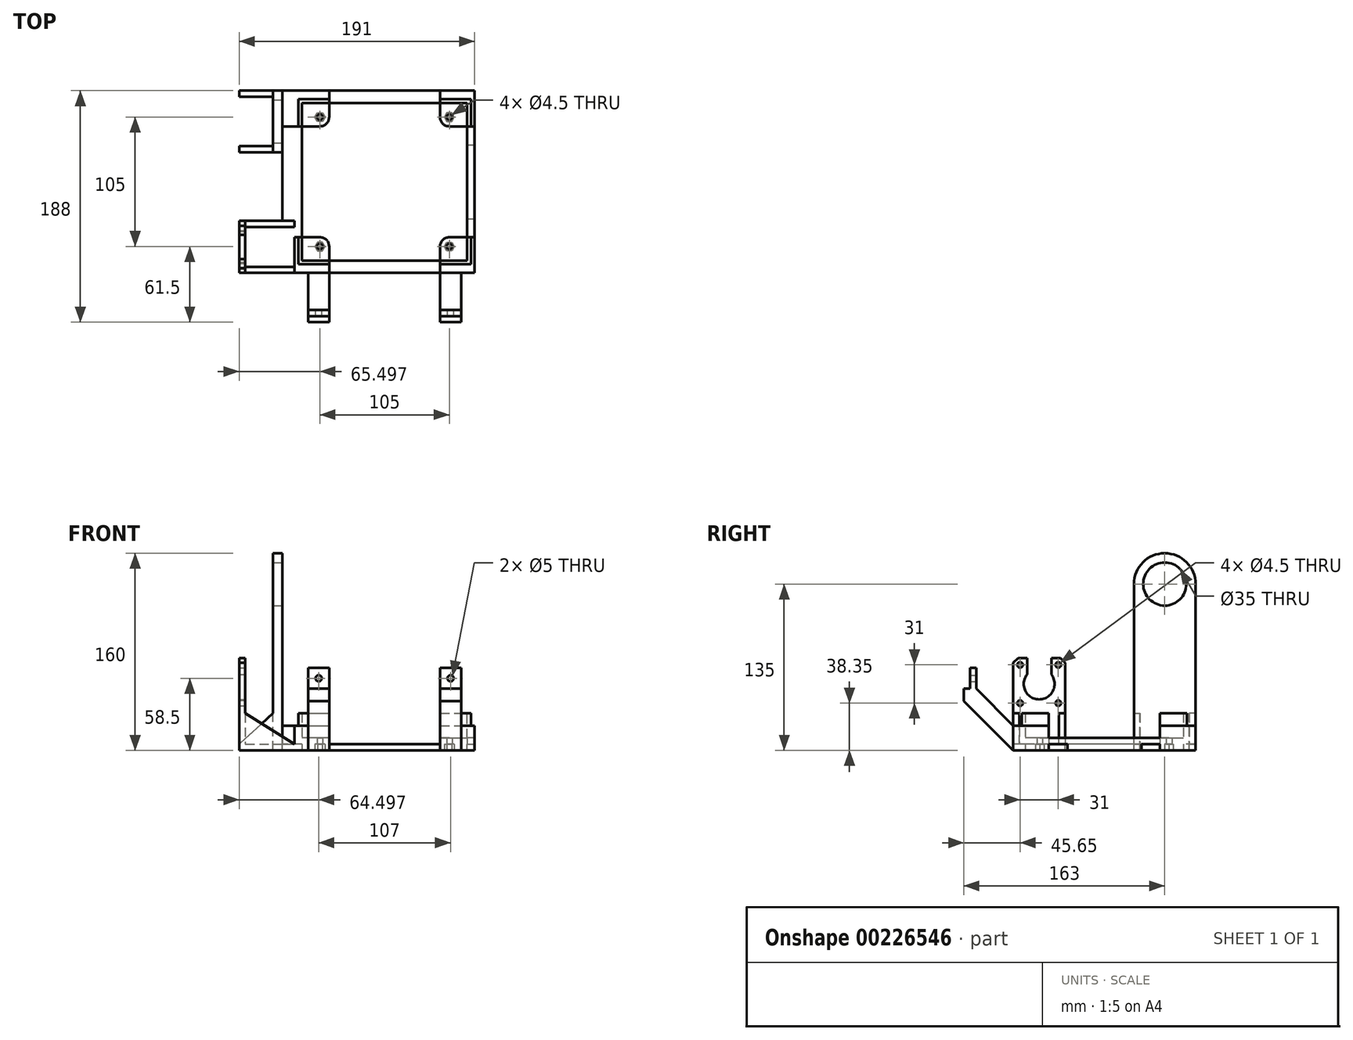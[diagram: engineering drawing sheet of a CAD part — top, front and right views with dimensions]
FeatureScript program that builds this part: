
annotation { "Feature Type Name" : "Feature", "Feature Type Description" : "" }
export const myFeature = defineFeature(function(context is Context, id is Id, definition is map)
    precondition{}
    {
        {
            var Q0;
            Q0=qCreatedBy(makeId("Top.planeOp"),FACE);
            var sketch = newSketch(context, id + "F0", { "sketchPlane" : qUnion([Q0])});
            skLineSegment(sketch, "E0.bottom", {"start": v(3.28, 0) * mm, "end": v(149.28, 0) * mm});
            skLineSegment(sketch, "E0.top", {"start": v(3.28, 148) * mm, "end": v(149.28, 148) * mm});
            skLineSegment(sketch, "E0.left", {"start": v(3.28, 0) * mm, "end": v(3.28, 148) * mm});
            skLineSegment(sketch, "E0.right", {"start": v(149.28, 0) * mm, "end": v(149.28, 148) * mm});
            skLineSegment(sketch, "E1.bottom", {"start": v(9.28, 10) * mm, "end": v(143.28, 10) * mm});
            skLineSegment(sketch, "E1.top", {"start": v(9.28, 138) * mm, "end": v(143.28, 138) * mm});
            skLineSegment(sketch, "E1.left", {"start": v(9.28, 10) * mm, "end": v(9.28, 138) * mm});
            skLineSegment(sketch, "E1.right", {"start": v(143.28, 10) * mm, "end": v(143.28, 138) * mm});
            skSolve(sketch);
        }
        {
            var Q0;
            Q0 = qSketchRegion(id + "F0", true);
            extrude(context, id + "F1", {"entities" : qUnion([Q0]), "depth" : 20 * mm});
        }
        {
            var Q0;
            Q0=makeQuery(id+"F1.opExtrude","CAP_FACE",FACE,{"disambiguationData":[OSD([sQuery(id+"F0.wireOp",EDGE,"E0.bottom"),sQuery(id+"F0.wireOp",EDGE,"E0.top"),sQuery(id+"F0.wireOp",EDGE,"E0.left"),sQuery(id+"F0.wireOp",EDGE,"E0.right"),sQuery(id+"F0.wireOp",EDGE,"E1.bottom"),sQuery(id+"F0.wireOp",EDGE,"E1.top"),sQuery(id+"F0.wireOp",EDGE,"E1.left"),sQuery(id+"F0.wireOp",EDGE,"E1.right")])],"isStart":false});
            var sketch = newSketch(context, id + "F2", { "sketchPlane" : qUnion([Q0])});
            skLineSegment(sketch, "E2.0", {"start": v(6.28, 141) * mm, "end": v(146.28, 141) * mm});
            skLineSegment(sketch, "E2.1", {"start": v(6.28, 7) * mm, "end": v(6.28, 141) * mm});
            skLineSegment(sketch, "E2.2", {"start": v(6.28, 7) * mm, "end": v(146.28, 7) * mm});
            skLineSegment(sketch, "E2.3", {"start": v(146.28, 7) * mm, "end": v(146.28, 141) * mm});
            skLineSegment(sketch, "E3.0", {"start": v(9.28, 10) * mm, "end": v(9.28, 138) * mm});
            skLineSegment(sketch, "E4.0", {"start": v(9.28, 138) * mm, "end": v(143.28, 138) * mm});
            skLineSegment(sketch, "E5.0", {"start": v(143.28, 10) * mm, "end": v(143.28, 138) * mm});
            skLineSegment(sketch, "E6.0", {"start": v(9.28, 10) * mm, "end": v(143.28, 10) * mm});
            skSolve(sketch);
        }
        {
            var Q0;
            Q0 = qSketchRegion(id + "F2", true);
            extrude(context, id + "F3", {"entities" : qUnion([Q0]), "operationType" : NewBodyOperationType.ADD, "depth" : 10 * mm});
        }
        {
            var Q0;
            Q0=qCreatedBy(makeId("Right.planeOp"),FACE);
            var sketch = newSketch(context, id + "F4", { "sketchPlane" : qUnion([Q0])});
            skLineSegment(sketch, "E7.0", {"start": v(7, 30) * mm, "end": v(141, 30) * mm, "construction": true});
            skPoint(sketch, "E8.0", {"position": v(141, 25) * mm});
            skLineSegment(sketch, "E9.0", {"start": v(141, 30) * mm, "end": v(141, 20) * mm, "construction": true});
            skLineSegment(sketch, "E10.0", {"start": v(0, 20) * mm, "end": v(148, 20) * mm, "construction": true});
            skLineSegment(sketch, "E11.0", {"start": v(148, 20) * mm, "end": v(148, 0) * mm, "construction": true});
            skLineSegment(sketch, "E12.0", {"start": v(0, 0) * mm, "end": v(148, 0) * mm, "construction": true});
            skLineSegment(sketch, "E13.0", {"start": v(0, 20) * mm, "end": v(0, 0) * mm, "construction": true});
            skLineSegment(sketch, "E14.0", {"start": v(7, 30) * mm, "end": v(7, 20) * mm, "construction": true});
            skLineSegment(sketch, "E15", {"start": v(119, 30) * mm, "end": v(119, 5) * mm});
            skLineSegment(sketch, "E16", {"start": v(119, 5) * mm, "end": v(29, 5) * mm});
            skLineSegment(sketch, "E17", {"start": v(29, 5) * mm, "end": v(29, 30) * mm});
            skLineSegment(sketch, "E18", {"start": v(29, 30) * mm, "end": v(119, 30) * mm});
            skSolve(sketch);
        }
        {
            var Q0;
            Q0 = qSketchRegion(id + "F4", true);
            extrude(context, id + "F5", {"entities" : qUnion([Q0]), "operationType" : NewBodyOperationType.REMOVE, "endBound" : BoundingType.THROUGH_ALL, "depth" : 25 * mm});
        }
        {
            var Q0;
            Q0=qCreatedBy(makeId("Front.planeOp"),FACE);
            var sketch = newSketch(context, id + "F6", { "sketchPlane" : qUnion([Q0])});
            skLineSegment(sketch, "E19.0", {"start": v(6.28, 30) * mm, "end": v(6.28, 20) * mm, "construction": true});
            skLineSegment(sketch, "E20.0", {"start": v(6.28, 30) * mm, "end": v(146.28, 30) * mm, "construction": true});
            skLineSegment(sketch, "E21.0", {"start": v(3.28, 20) * mm, "end": v(3.28, 0) * mm, "construction": true});
            skLineSegment(sketch, "E22.0", {"start": v(3.28, 20) * mm, "end": v(149.28, 20) * mm, "construction": true});
            skLineSegment(sketch, "E23.0", {"start": v(146.28, 30) * mm, "end": v(146.28, 20) * mm, "construction": true});
            skLineSegment(sketch, "E24.0", {"start": v(149.28, 20) * mm, "end": v(149.28, 0) * mm, "construction": true});
            skLineSegment(sketch, "E25", {"start": v(31.28, 30) * mm, "end": v(121.28, 30) * mm});
            skLineSegment(sketch, "E26", {"start": v(31.28, 5) * mm, "end": v(31.28, 30) * mm});
            skLineSegment(sketch, "E27", {"start": v(31.28, 5) * mm, "end": v(121.28, 5) * mm});
            skLineSegment(sketch, "E28", {"start": v(121.28, 5) * mm, "end": v(121.28, 30) * mm});
            skSolve(sketch);
        }
        {
            var Q0;
            Q0 = qSketchRegion(id + "F6", true);
            extrude(context, id + "F7", {"entities" : qUnion([Q0]), "operationType" : NewBodyOperationType.REMOVE, "endBound" : BoundingType.THROUGH_ALL, "oppositeDirection" : true, "depth" : 25 * mm});
        }
        {
            var Q0;
            Q0=makeQuery(id+"F1.opExtrude","SWEPT_FACE",FACE,{"disambiguationData":[OSD([sQuery(id+"F0.wireOp",EDGE,"E0.bottom")])]});
            var sketch = newSketch(context, id + "F8", { "sketchPlane" : qUnion([Q0])});
            skPoint(sketch, "E29.firstSnap0", {"position": v(31.28, 12.5) * mm});
            skLineSegment(sketch, "E29.bottom", {"start": v(31.28, 0) * mm, "end": v(14.28, 0) * mm});
            skLineSegment(sketch, "E29.top", {"start": v(31.28, 67) * mm, "end": v(14.28, 67) * mm});
            skLineSegment(sketch, "E29.left", {"start": v(31.28, 0) * mm, "end": v(31.28, 67) * mm});
            skLineSegment(sketch, "E29.right", {"start": v(14.28, 0) * mm, "end": v(14.28, 67) * mm});
            skLineSegment(sketch, "E30.bottom", {"start": v(121.28, 0) * mm, "end": v(138.28, 0) * mm});
            skLineSegment(sketch, "E30.top", {"start": v(121.28, 67) * mm, "end": v(138.28, 67) * mm});
            skLineSegment(sketch, "E30.left", {"start": v(121.28, 0) * mm, "end": v(121.28, 67) * mm});
            skLineSegment(sketch, "E30.right", {"start": v(138.28, 0) * mm, "end": v(138.28, 67) * mm});
            skLineSegment(sketch, "E31.0", {"start": v(6.28, 30) * mm, "end": v(31.28, 30) * mm, "construction": true});
            skCircle(sketch, "E32", {"center": v(22.78, 58.5) * mm, "radius": 2.5 * mm});
            skCircle(sketch, "E33", {"center": v(129.78, 58.5) * mm, "radius": 2.5 * mm});
            skSolve(sketch);
        }
        {
            var Q0;
            Q0 = qSketchRegion(id + "F8", true);
            extrude(context, id + "F9", {"entities" : qUnion([Q0]), "operationType" : NewBodyOperationType.ADD, "depth" : 40 * mm});
        }
        {
            var Q0;
            Q0=makeQuery(id+"F9.opExtrude","SWEPT_FACE",FACE,{"disambiguationData":[OSD([sQuery(id+"F8.wireOp",EDGE,"E29.right")])]});
            var sketch = newSketch(context, id + "F10", { "sketchPlane" : qUnion([Q0])});
            skLineSegment(sketch, "E34", {"start": v(0, 20) * mm, "end": v(30, 50) * mm});
            skLineSegment(sketch, "E35", {"start": v(30, 50) * mm, "end": v(30, 67) * mm});
            skLineSegment(sketch, "E36", {"start": v(30, 67) * mm, "end": v(0, 67) * mm});
            skLineSegment(sketch, "E37", {"start": v(0, 67) * mm, "end": v(0, 20) * mm});
            skLineSegment(sketch, "E38.bottom", {"start": v(40, 67) * mm, "end": v(35, 67) * mm});
            skLineSegment(sketch, "E38.top", {"start": v(40, 50) * mm, "end": v(35, 50) * mm});
            skLineSegment(sketch, "E38.left", {"start": v(40, 67) * mm, "end": v(40, 50) * mm});
            skLineSegment(sketch, "E38.right", {"start": v(35, 67) * mm, "end": v(35, 50) * mm});
            skLineSegment(sketch, "E39", {"start": v(0, 0) * mm, "end": v(40, 40) * mm});
            skLineSegment(sketch, "E40", {"start": v(40, 40) * mm, "end": v(40, 0) * mm});
            skLineSegment(sketch, "E41", {"start": v(40, 0) * mm, "end": v(0, 0) * mm});
            skSolve(sketch);
        }
        {
            var Q0;
            Q0 = qSketchRegion(id + "F10", true);
            extrude(context, id + "F11", {"entities" : qUnion([Q0]), "operationType" : NewBodyOperationType.REMOVE, "endBound" : BoundingType.THROUGH_ALL, "oppositeDirection" : true, "depth" : 25 * mm});
        }
        {
            var Q0;
            Q0=makeQuery(id+"F1.opExtrude","SWEPT_FACE",FACE,{"disambiguationData":[OSD([sQuery(id+"F0.wireOp",EDGE,"E0.left")])]});
            var sketch = newSketch(context, id + "F12", { "sketchPlane" : qUnion([Q0])});
            skLineSegment(sketch, "E42.bottom", {"start": v(0, 0) * mm, "end": v(-148, 0) * mm});
            skLineSegment(sketch, "E42.top", {"start": v(0, 5) * mm, "end": v(-148, 5) * mm});
            skLineSegment(sketch, "E42.left", {"start": v(0, 0) * mm, "end": v(0, 5) * mm});
            skLineSegment(sketch, "E42.right", {"start": v(-148, 0) * mm, "end": v(-148, 5) * mm});
            skSolve(sketch);
        }
        {
            var Q0;
            Q0 = qSketchRegion(id + "F12", true);
            extrude(context, id + "F13", {"entities" : qUnion([Q0]), "operationType" : NewBodyOperationType.ADD, "depth" : 10 * mm});
        }
        {
            var Q0;
            Q0=makeQuery(id+"F13.opExtrude","CAP_FACE",FACE,{"disambiguationData":[OSD([sQuery(id+"F12.wireOp",EDGE,"E42.bottom"),sQuery(id+"F12.wireOp",EDGE,"E42.top"),sQuery(id+"F12.wireOp",EDGE,"E42.left"),sQuery(id+"F12.wireOp",EDGE,"E42.right")])],"isStart":false});
            var sketch = newSketch(context, id + "F14", { "sketchPlane" : qUnion([Q0])});
            skLineSegment(sketch, "E43.bottom", {"start": v(-148, 0) * mm, "end": v(-98, 0) * mm});
            skLineSegment(sketch, "E43.left", {"start": v(-148, 0) * mm, "end": v(-148, 135) * mm});
            skLineSegment(sketch, "E43.right", {"start": v(-98, 0) * mm, "end": v(-98, 135) * mm});
            skArc(sketch, "E44", {"start": v(-98, 135) * mm, "mid": v(-123, 160) * mm, "end": v(-148, 135) * mm});
            skCircle(sketch, "E45", {"center": v(-123, 135) * mm, "radius": 17.5 * mm});
            skSolve(sketch);
        }
        {
            var Q0;
            Q0 = qSketchRegion(id + "F14", true);
            extrude(context, id + "F15", {"entities" : qUnion([Q0]), "operationType" : NewBodyOperationType.ADD, "depth" : 7.5 * mm});
        }
        {
            var Q0;
            Q0=makeQuery(id+"F13.boolean.opBoolean","MERGE",FACE,{"derivedFrom":[makeQuery(id+"F5.boolean.opBoolean","COPY",FACE,{"disambiguationData":[TD([makeQuery(id+"F1.opExtrude","SWEPT_FACE",FACE,{"disambiguationData":[OSD([sQuery(id+"F0.wireOp",EDGE,"E0.left")])]})])],"derivedFrom":makeQuery(id+"F5.opExtrude","SWEPT_FACE",FACE,{"disambiguationData":[OSD([sQuery(id+"F4.wireOp",EDGE,"E16")])]})}),makeQuery(id+"F13.opExtrude","SWEPT_FACE",FACE,{"disambiguationData":[OSD([sQuery(id+"F12.wireOp",EDGE,"E42.top")])]})]});
            var sketch = newSketch(context, id + "F16", { "sketchPlane" : qUnion([Q0])});
            skLineSegment(sketch, "E46.bottom", {"start": v(3.28, 148) * mm, "end": v(-6.72, 148) * mm});
            skLineSegment(sketch, "E46.top", {"start": v(3.28, 119) * mm, "end": v(-6.72, 119) * mm});
            skLineSegment(sketch, "E46.left", {"start": v(3.28, 148) * mm, "end": v(3.28, 119) * mm});
            skLineSegment(sketch, "E46.right", {"start": v(-6.72, 148) * mm, "end": v(-6.72, 119) * mm});
            skSolve(sketch);
        }
        {
            var Q0;
            Q0 = qSketchRegion(id + "F16", true);
            var Q1;
            {var subQ4=sQuery(id+"F0.wireOp",EDGE,"E0.left");var subQ5=makeQuery(id+"F1.opExtrude","SWEPT_FACE",FACE,{"disambiguationData":[OSD([subQ4])]});var subQ6=sQuery(id+"F0.wireOp",EDGE,"E0.top");var subQ7=makeQuery(id+"F1.opExtrude","SWEPT_FACE",FACE,{"disambiguationData":[OSD([subQ6])]});var subQ10=sQuery(id+"F0.wireOp",EDGE,"E1.left");var subQ11=sQuery(id+"F0.wireOp",EDGE,"E0.right");var subQ12=makeQuery(id+"F1.opExtrude","CAP_FACE",FACE,{"disambiguationData":[OSD([sQuery(id+"F0.wireOp",EDGE,"E0.bottom"),subQ6,subQ4,subQ11,sQuery(id+"F0.wireOp",EDGE,"E1.bottom"),sQuery(id+"F0.wireOp",EDGE,"E1.top"),subQ10,sQuery(id+"F0.wireOp",EDGE,"E1.right")])],"isStart":false});Q1=makeQuery(id+"F7.boolean.opBoolean","SPLIT",FACE,{"disambiguationData":[TD([subQ5])],"derivedFrom":makeQuery(id+"F5.boolean.opBoolean","SPLIT",FACE,{"disambiguationData":[TD([subQ7])],"derivedFrom":subQ12})});}
            extrude(context, id + "F17", {"entities" : qUnion([Q0]), "operationType" : NewBodyOperationType.ADD, "endBound" : BoundingType.UP_TO_SURFACE, "endBoundEntityFace" : qUnion([Q1]), "depth" : 25 * mm});
        }
        {
            var Q0;
            Q0=makeQuery(id+"F5.boolean.opBoolean","COPY",FACE,{"disambiguationData":[TD([makeQuery(id+"F1.opExtrude","SWEPT_FACE",FACE,{"disambiguationData":[OSD([sQuery(id+"F0.wireOp",EDGE,"E0.right")])]})])],"derivedFrom":makeQuery(id+"F5.opExtrude","SWEPT_FACE",FACE,{"disambiguationData":[OSD([sQuery(id+"F4.wireOp",EDGE,"E16")])]})});
            var sketch = newSketch(context, id + "F18", { "sketchPlane" : qUnion([Q0])});
            skLineSegment(sketch, "E47.bottom", {"start": v(143.28, 119) * mm, "end": v(149.28, 119) * mm});
            skLineSegment(sketch, "E47.top", {"start": v(143.28, 29) * mm, "end": v(149.28, 29) * mm});
            skLineSegment(sketch, "E47.left", {"start": v(143.28, 119) * mm, "end": v(143.28, 29) * mm});
            skLineSegment(sketch, "E47.right", {"start": v(149.28, 119) * mm, "end": v(149.28, 29) * mm});
            skSolve(sketch);
        }
        {
            var Q0;
            Q0 = qSketchRegion(id + "F18", true);
            extrude(context, id + "F19", {"entities" : qUnion([Q0]), "operationType" : NewBodyOperationType.ADD, "depth" : 5 * mm});
        }
        {
            var Q0;
            Q0=makeQuery(id+"F19.boolean.opBoolean","MERGE",FACE,{"derivedFrom":[makeQuery(id+"F1.opExtrude","SWEPT_FACE",FACE,{"disambiguationData":[OSD([sQuery(id+"F0.wireOp",EDGE,"E0.right")])]}),makeQuery(id+"F19.opExtrude","SWEPT_FACE",FACE,{"disambiguationData":[OSD([sQuery(id+"F18.wireOp",EDGE,"E47.right")])]})]});
            var sketch = newSketch(context, id + "F20", { "sketchPlane" : qUnion([Q0])});
            skLineSegment(sketch, "E48.bottom", {"start": v(29, 0) * mm, "end": v(44, 0) * mm});
            skLineSegment(sketch, "E48.top", {"start": v(29, 5) * mm, "end": v(44, 5) * mm});
            skLineSegment(sketch, "E48.left", {"start": v(29, 0) * mm, "end": v(29, 5) * mm});
            skLineSegment(sketch, "E48.right", {"start": v(44, 0) * mm, "end": v(44, 5) * mm});
            skLineSegment(sketch, "E49.bottom", {"start": v(119, 0) * mm, "end": v(104, 0) * mm});
            skLineSegment(sketch, "E49.top", {"start": v(119, 5) * mm, "end": v(104, 5) * mm});
            skLineSegment(sketch, "E49.left", {"start": v(119, 0) * mm, "end": v(119, 5) * mm});
            skLineSegment(sketch, "E49.right", {"start": v(104, 0) * mm, "end": v(104, 5) * mm});
            skSolve(sketch);
        }
        {
            var Q0;
            Q0 = qSketchRegion(id + "F20", true);
            extrude(context, id + "F21", {"entities" : qUnion([Q0]), "operationType" : NewBodyOperationType.REMOVE, "endBound" : BoundingType.UP_TO_NEXT, "oppositeDirection" : true, "depth" : 25 * mm});
        }
        {
            var Q0;
            {var subQ5=makeQuery(id+"F13.opExtrude","CAP_EDGE",EDGE,{"disambiguationData":[OSD([sQuery(id+"F12.wireOp",EDGE,"E42.left")])],"isStart":false});Q0=makeQuery(id+"F14.imprint","IMPRINT",FACE,{"disambiguationData":[TD([[makeQuery(id+"F14.imprint","IMPRINT",EDGE,{"derivedFrom":subQ5}),-1.0]])]});}
            var sketch = newSketch(context, id + "F22", { "sketchPlane" : qUnion([Q0])});
            skLineSegment(sketch, "E50.0", {"start": v(0, 5) * mm, "end": v(-148, 5) * mm, "construction": true});
            skLineSegment(sketch, "E51.0", {"start": v(0, 0) * mm, "end": v(0, 5) * mm, "construction": true});
            skLineSegment(sketch, "E52.0", {"start": v(-10, 0) * mm, "end": v(-138, 0) * mm, "construction": true});
            skSolve(sketch);
        }
        {
            var Q0;
            {var subQ5=makeQuery(id+"F13.opExtrude","CAP_EDGE",EDGE,{"disambiguationData":[OSD([sQuery(id+"F12.wireOp",EDGE,"E42.left")])],"isStart":false});Q0=makeQuery(id+"F14.imprint","IMPRINT",FACE,{"disambiguationData":[TD([[makeQuery(id+"F14.imprint","IMPRINT",EDGE,{"derivedFrom":subQ5}),-1.0]])]});}
            var sketch = newSketch(context, id + "F23", { "sketchPlane" : qUnion([Q0])});
            skLineSegment(sketch, "E53.bottom", {"start": v(0, 0) * mm, "end": v(-42.3, 0) * mm});
            skLineSegment(sketch, "E53.top", {"start": v(0, 5) * mm, "end": v(-42.3, 5) * mm});
            skLineSegment(sketch, "E53.left", {"start": v(0, 0) * mm, "end": v(0, 5) * mm});
            skLineSegment(sketch, "E53.right", {"start": v(-42.3, 0) * mm, "end": v(-42.3, 5) * mm});
            skSolve(sketch);
        }
        {
            var Q0;
            Q0 = qSketchRegion(id + "F23", true);
            extrude(context, id + "F24", {"entities" : qUnion([Q0]), "operationType" : NewBodyOperationType.ADD, "depth" : 30 * mm});
        }
        {
            var Q0;
            Q0=makeQuery(id+"F24.opExtrude","CAP_FACE",FACE,{"disambiguationData":[OSD([sQuery(id+"F23.wireOp",EDGE,"E53.bottom"),sQuery(id+"F23.wireOp",EDGE,"E53.top"),sQuery(id+"F23.wireOp",EDGE,"E53.left"),sQuery(id+"F23.wireOp",EDGE,"E53.right")])],"isStart":false});
            var sketch = newSketch(context, id + "F25", { "sketchPlane" : qUnion([Q0])});
            skLineSegment(sketch, "E54.bottom", {"start": v(-42.3, 0) * mm, "end": v(0, 0) * mm});
            skLineSegment(sketch, "E54.top", {"start": v(-42.3, 75) * mm, "end": v(-31, 75) * mm});
            skLineSegment(sketch, "E54.left", {"start": v(-42.3, 0) * mm, "end": v(-42.3, 75) * mm});
            skLineSegment(sketch, "E54.right", {"start": v(0, 0) * mm, "end": v(0, 75) * mm});
            skLineSegment(sketch, "E55.left", {"start": v(-31, 75) * mm, "end": v(-31, 61.55) * mm});
            skLineSegment(sketch, "E55.right", {"start": v(-11.3, 75) * mm, "end": v(-11.3, 61.55) * mm});
            skArc(sketch, "E56", {"start": v(-31, 61.55) * mm, "mid": v(-21.15, 41.35) * mm, "end": v(-11.3, 61.55) * mm});
            skLineSegment(sketch, "E57", {"start": v(-11.3, 75) * mm, "end": v(0, 75) * mm});
            skCircle(sketch, "E58", {"center": v(-36.65, 69.35) * mm, "radius": 2.25 * mm});
            skCircle(sketch, "E59", {"center": v(-36.65, 38.35) * mm, "radius": 2.25 * mm});
            skCircle(sketch, "E60", {"center": v(-5.65, 69.35) * mm, "radius": 2.25 * mm});
            skCircle(sketch, "E61", {"center": v(-5.65, 38.35) * mm, "radius": 2.25 * mm});
            skSolve(sketch);
        }
        {
            var Q0;
            Q0 = qSketchRegion(id + "F25", true);
            extrude(context, id + "F26", {"entities" : qUnion([Q0]), "operationType" : NewBodyOperationType.ADD, "depth" : 5 * mm});
        }
        {
            var Q0;
            Q0=makeQuery(id+"F26.opExtrude","SWEPT_EDGE",EDGE,{"disambiguationData":[OSD([sQuery(id+"F25.wireOp",EDGE,"E54.top"),sQuery(id+"F25.wireOp",EDGE,"E54.left")])]});
            var Q1;
            Q1=makeQuery(id+"F26.opExtrude","SWEPT_EDGE",EDGE,{"disambiguationData":[OSD([sQuery(id+"F25.wireOp",EDGE,"E54.right"),sQuery(id+"F25.wireOp",EDGE,"E57")])]});
            chamfer(context, id + "F27", {"entities" : qUnion([Q0, Q1]), "width" : 4 * mm, "tangentPropagation" : true});
        }
        {
            var Q0;
            Q0=makeQuery(id+"F24.boolean.opBoolean","MERGE",FACE,{"derivedFrom":[makeQuery(id+"F13.boolean.opBoolean","MERGE",FACE,{"derivedFrom":[makeQuery(id+"F5.boolean.opBoolean","COPY",FACE,{"disambiguationData":[TD([makeQuery(id+"F1.opExtrude","SWEPT_FACE",FACE,{"disambiguationData":[OSD([sQuery(id+"F0.wireOp",EDGE,"E0.left")])]})])],"derivedFrom":makeQuery(id+"F5.opExtrude","SWEPT_FACE",FACE,{"disambiguationData":[OSD([sQuery(id+"F4.wireOp",EDGE,"E16")])]})}),makeQuery(id+"F13.opExtrude","SWEPT_FACE",FACE,{"disambiguationData":[OSD([sQuery(id+"F12.wireOp",EDGE,"E42.top")])]})]}),makeQuery(id+"F24.opExtrude","SWEPT_FACE",FACE,{"disambiguationData":[OSD([sQuery(id+"F23.wireOp",EDGE,"E53.top")])]})]});
            var sketch = newSketch(context, id + "F28", { "sketchPlane" : qUnion([Q0])});
            skLineSegment(sketch, "E62.bottom", {"start": v(-36.72, 42.3) * mm, "end": v(3.28, 42.3) * mm});
            skLineSegment(sketch, "E62.top", {"start": v(-36.72, 37.3) * mm, "end": v(3.28, 37.3) * mm});
            skLineSegment(sketch, "E62.left", {"start": v(-36.72, 42.3) * mm, "end": v(-36.72, 37.3) * mm});
            skLineSegment(sketch, "E62.right", {"start": v(3.28, 42.3) * mm, "end": v(3.28, 37.3) * mm});
            skLineSegment(sketch, "E63.bottom", {"start": v(-36.72, 0) * mm, "end": v(3.28, 0) * mm});
            skLineSegment(sketch, "E63.top", {"start": v(-36.72, 5) * mm, "end": v(3.28, 5) * mm});
            skLineSegment(sketch, "E63.left", {"start": v(-36.72, 0) * mm, "end": v(-36.72, 5) * mm});
            skLineSegment(sketch, "E63.right", {"start": v(3.28, 0) * mm, "end": v(3.28, 5) * mm});
            skSolve(sketch);
        }
        {
            var Q0;
            Q0 = qSketchRegion(id + "F28", true);
            extrude(context, id + "F29", {"entities" : qUnion([Q0]), "operationType" : NewBodyOperationType.ADD, "depth" : 25 * mm});
        }
        {
            var Q0;
            {var subQ1=sQuery(id+"F0.wireOp",EDGE,"E0.left");var subQ9=sQuery(id+"F0.wireOp",EDGE,"E0.bottom");Q0=makeQuery(id+"F29.boolean.opBoolean","MERGE",FACE,{"derivedFrom":[makeQuery(id+"F26.boolean.opBoolean","MERGE",FACE,{"derivedFrom":[makeQuery(id+"F24.boolean.opBoolean","MERGE",FACE,{"derivedFrom":[makeQuery(id+"F13.boolean.opBoolean","MERGE",FACE,{"derivedFrom":[makeQuery(id+"F9.boolean.opBoolean","SPLIT",FACE,{"disambiguationData":[TD([makeQuery(id+"F1.opExtrude","SWEPT_FACE",FACE,{"disambiguationData":[OSD([subQ1])]})])],"derivedFrom":makeQuery(id+"F1.opExtrude","SWEPT_FACE",FACE,{"disambiguationData":[OSD([subQ9])]})}),makeQuery(id+"F13.opExtrude","SWEPT_FACE",FACE,{"disambiguationData":[OSD([sQuery(id+"F12.wireOp",EDGE,"E42.left")])]})]}),makeQuery(id+"F24.opExtrude","SWEPT_FACE",FACE,{"disambiguationData":[OSD([sQuery(id+"F23.wireOp",EDGE,"E53.left")])]})]}),makeQuery(id+"F26.opExtrude","SWEPT_FACE",FACE,{"disambiguationData":[OSD([sQuery(id+"F25.wireOp",EDGE,"E54.right")])]})]}),makeQuery(id+"F29.opExtrude","SWEPT_FACE",FACE,{"disambiguationData":[OSD([sQuery(id+"F28.wireOp",EDGE,"E63.bottom")])]})]});}
            var sketch = newSketch(context, id + "F30", { "sketchPlane" : qUnion([Q0])});
            skLineSegment(sketch, "E64.0.1", {"start": v(-36.72, 5) * mm, "end": v(3.28, 5) * mm, "construction": true});
            skLineSegment(sketch, "E64.0.3", {"start": v(3.28, 5) * mm, "end": v(9.28, 5) * mm, "construction": true});
            skLineSegment(sketch, "E64.0.5", {"start": v(9.28, 5) * mm, "end": v(-6.72, 5) * mm, "construction": true});
            skLineSegment(sketch, "E64.0.8", {"start": v(-6.72, 5) * mm, "end": v(3.28, 5) * mm, "construction": true});
            skLineSegment(sketch, "E64.0.10", {"start": v(3.28, 5) * mm, "end": v(-36.72, 5) * mm, "construction": true});
            skLineSegment(sketch, "E65", {"start": v(-36.72, 30) * mm, "end": v(3.28, 5) * mm});
            skLineSegment(sketch, "E66", {"start": v(3.28, 30) * mm, "end": v(-36.72, 30) * mm});
            skLineSegment(sketch, "E67", {"start": v(3.28, 30) * mm, "end": v(3.28, 5) * mm});
            skSolve(sketch);
        }
        {
            var Q0;
            Q0 = qSketchRegion(id + "F30", true);
            var Q1;
            Q1=makeQuery(id+"F29.boolean.opBoolean","MERGE",FACE,{"derivedFrom":[makeQuery(id+"F26.boolean.opBoolean","MERGE",FACE,{"derivedFrom":[makeQuery(id+"F24.opExtrude","SWEPT_FACE",FACE,{"disambiguationData":[OSD([sQuery(id+"F23.wireOp",EDGE,"E53.right")])]}),makeQuery(id+"F26.opExtrude","SWEPT_FACE",FACE,{"disambiguationData":[OSD([sQuery(id+"F25.wireOp",EDGE,"E54.left")])]})]}),makeQuery(id+"F29.opExtrude","SWEPT_FACE",FACE,{"disambiguationData":[OSD([sQuery(id+"F28.wireOp",EDGE,"E62.bottom")])]})]});
            extrude(context, id + "F31", {"entities" : qUnion([Q0]), "operationType" : NewBodyOperationType.REMOVE, "endBound" : BoundingType.UP_TO_SURFACE, "oppositeDirection" : true, "endBoundEntityFace" : qUnion([Q1]), "depth" : 25 * mm});
        }
        {
            var Q0;
            Q0=makeQuery(id+"F15.opExtrude","CAP_FACE",FACE,{"disambiguationData":[OSD([sQuery(id+"F14.wireOp",EDGE,"E43.bottom"),sQuery(id+"F14.wireOp",EDGE,"E43.left"),sQuery(id+"F14.wireOp",EDGE,"E43.right"),sQuery(id+"F14.wireOp",EDGE,"E44"),sQuery(id+"F14.wireOp",EDGE,"E45")])],"isStart":false});
            var sketch = newSketch(context, id + "F32", { "sketchPlane" : qUnion([Q0])});
            skLineSegment(sketch, "E68.bottom", {"start": v(-148, 0) * mm, "end": v(-143, 0) * mm});
            skLineSegment(sketch, "E68.top", {"start": v(-148, 30) * mm, "end": v(-143, 30) * mm});
            skLineSegment(sketch, "E68.left", {"start": v(-148, 0) * mm, "end": v(-148, 30) * mm});
            skLineSegment(sketch, "E68.right", {"start": v(-143, 0) * mm, "end": v(-143, 30) * mm});
            skLineSegment(sketch, "E69.bottom", {"start": v(-98, 0) * mm, "end": v(-103, 0) * mm});
            skLineSegment(sketch, "E69.top", {"start": v(-98, 30) * mm, "end": v(-103, 30) * mm});
            skLineSegment(sketch, "E69.left", {"start": v(-98, 0) * mm, "end": v(-98, 30) * mm});
            skLineSegment(sketch, "E69.right", {"start": v(-103, 0) * mm, "end": v(-103, 30) * mm});
            skSolve(sketch);
        }
        {
            var Q0;
            Q0 = qSketchRegion(id + "F32", true);
            var Q1;
            Q1=makeQuery(id+"F26.opExtrude","CAP_FACE",FACE,{"disambiguationData":[OSD([sQuery(id+"F25.wireOp",EDGE,"E54.bottom"),sQuery(id+"F25.wireOp",EDGE,"E54.top"),sQuery(id+"F25.wireOp",EDGE,"E54.left"),sQuery(id+"F25.wireOp",EDGE,"E54.right"),sQuery(id+"F25.wireOp",EDGE,"E55.left"),sQuery(id+"F25.wireOp",EDGE,"E55.right"),sQuery(id+"F25.wireOp",EDGE,"E56"),sQuery(id+"F25.wireOp",EDGE,"E57"),sQuery(id+"F25.wireOp",EDGE,"E58"),sQuery(id+"F25.wireOp",EDGE,"E59"),sQuery(id+"F25.wireOp",EDGE,"E60"),sQuery(id+"F25.wireOp",EDGE,"E61")])],"isStart":false});
            extrude(context, id + "F33", {"entities" : qUnion([Q0]), "operationType" : NewBodyOperationType.ADD, "endBound" : BoundingType.UP_TO_SURFACE, "endBoundEntityFace" : qUnion([Q1]), "depth" : 25 * mm});
        }
        {
            var Q0;
            Q0=makeQuery(id+"F33.boolean.opBoolean","MERGE",FACE,{"derivedFrom":[makeQuery(id+"F17.boolean.opBoolean","MERGE",FACE,{"derivedFrom":[makeQuery(id+"F15.boolean.opBoolean","MERGE",FACE,{"derivedFrom":[makeQuery(id+"F13.boolean.opBoolean","MERGE",FACE,{"derivedFrom":[makeQuery(id+"F1.opExtrude","SWEPT_FACE",FACE,{"disambiguationData":[OSD([sQuery(id+"F0.wireOp",EDGE,"E0.top")])]}),makeQuery(id+"F13.opExtrude","SWEPT_FACE",FACE,{"disambiguationData":[OSD([sQuery(id+"F12.wireOp",EDGE,"E42.right")])]})]}),makeQuery(id+"F15.opExtrude","SWEPT_FACE",FACE,{"disambiguationData":[OSD([sQuery(id+"F14.wireOp",EDGE,"E43.left")])]})]}),makeQuery(id+"F17.opExtrude","SWEPT_FACE",FACE,{"disambiguationData":[OSD([sQuery(id+"F16.wireOp",EDGE,"E46.bottom")])]})]}),makeQuery(id+"F33.opExtrude","SWEPT_FACE",FACE,{"disambiguationData":[OSD([sQuery(id+"F32.wireOp",EDGE,"E68.left")])]})]});
            var sketch = newSketch(context, id + "F34", { "sketchPlane" : qUnion([Q0])});
            skLineSegment(sketch, "E70", {"start": v(41.72, 30) * mm, "end": v(14.22, 30) * mm});
            skLineSegment(sketch, "E71", {"start": v(14.22, 30) * mm, "end": v(41.72, 5) * mm});
            skLineSegment(sketch, "E72", {"start": v(41.72, 5) * mm, "end": v(41.72, 30) * mm});
            skSolve(sketch);
        }
        {
            var Q0;
            Q0 = qSketchRegion(id + "F34", true);
            var Q1;
            Q1=makeQuery(id+"F33.boolean.opBoolean","MERGE",FACE,{"derivedFrom":[makeQuery(id+"F15.opExtrude","SWEPT_FACE",FACE,{"disambiguationData":[OSD([sQuery(id+"F14.wireOp",EDGE,"E43.right")])]}),makeQuery(id+"F33.opExtrude","SWEPT_FACE",FACE,{"disambiguationData":[OSD([sQuery(id+"F32.wireOp",EDGE,"E69.left")])]})]});
            extrude(context, id + "F35", {"entities" : qUnion([Q0]), "operationType" : NewBodyOperationType.REMOVE, "endBound" : BoundingType.UP_TO_SURFACE, "oppositeDirection" : true, "endBoundEntityFace" : qUnion([Q1]), "depth" : 25 * mm});
        }
        {
            var Q0;
            Q0=qCreatedBy(makeId("Top.planeOp"),FACE);
            var sketch = newSketch(context, id + "F36", { "sketchPlane" : qUnion([Q0])});
            skLineSegment(sketch, "E73.bottom", {"start": v(23.78, 21.5) * mm, "end": v(128.78, 21.5) * mm, "construction": true});
            skLineSegment(sketch, "E73.top", {"start": v(23.78, 126.5) * mm, "end": v(128.78, 126.5) * mm, "construction": true});
            skLineSegment(sketch, "E73.left", {"start": v(23.78, 21.5) * mm, "end": v(23.78, 126.5) * mm, "construction": true});
            skLineSegment(sketch, "E73.right", {"start": v(128.78, 21.5) * mm, "end": v(128.78, 126.5) * mm, "construction": true});
            skArc(sketch, "E74", {"start": v(31.28, 21.5) * mm, "mid": v(29.08, 26.8) * mm, "end": v(23.78, 29) * mm});
            skLineSegment(sketch, "E75.0.1", {"start": v(121.28, 10) * mm, "end": v(143.28, 10) * mm, "construction": true});
            skLineSegment(sketch, "E75.0.3", {"start": v(143.28, 10) * mm, "end": v(9.28, 10) * mm, "construction": true});
            skLineSegment(sketch, "E75.0.5", {"start": v(9.28, 10) * mm, "end": v(31.28, 10) * mm, "construction": true});
            skLineSegment(sketch, "E75.0.7", {"start": v(31.28, 10) * mm, "end": v(121.28, 10) * mm, "construction": true});
            skLineSegment(sketch, "E76.0.0", {"start": v(9.28, 119) * mm, "end": v(9.28, 29) * mm, "construction": true});
            skLineSegment(sketch, "E76.0.2", {"start": v(9.28, 29) * mm, "end": v(9.28, 10) * mm, "construction": true});
            skLineSegment(sketch, "E76.0.4", {"start": v(9.28, 10) * mm, "end": v(9.28, 138) * mm, "construction": true});
            skLineSegment(sketch, "E76.0.6", {"start": v(9.28, 138) * mm, "end": v(9.28, 119) * mm, "construction": true});
            skLineSegment(sketch, "E77", {"start": v(31.28, 21.5) * mm, "end": v(31.28, 10) * mm});
            skLineSegment(sketch, "E78", {"start": v(31.28, 10) * mm, "end": v(9.28, 10) * mm});
            skLineSegment(sketch, "E79", {"start": v(23.78, 29) * mm, "end": v(9.28, 29) * mm});
            skLineSegment(sketch, "E80", {"start": v(9.28, 29) * mm, "end": v(9.28, 10) * mm});
            skLineSegment(sketch, "E81", {"start": v(76.28, 21.5) * mm, "end": v(76.28, 126.5) * mm, "construction": true});
            skLineSegment(sketch, "E82", {"start": v(23.78, 74) * mm, "end": v(128.78, 74) * mm, "construction": true});
            skLineSegment(sketch, "E83.MirrorCS", {"start": v(121.28, 10) * mm, "end": v(143.28, 10) * mm});
            skLineSegment(sketch, "E84.MirrorCS", {"start": v(143.28, 29) * mm, "end": v(143.28, 10) * mm});
            skLineSegment(sketch, "E85.MirrorCS", {"start": v(143.28, 119) * mm, "end": v(143.28, 29) * mm, "construction": true});
            skLineSegment(sketch, "E86.MirrorCS", {"start": v(143.28, 29) * mm, "end": v(143.28, 10) * mm, "construction": true});
            skLineSegment(sketch, "E87.MirrorCS", {"start": v(143.28, 10) * mm, "end": v(121.28, 10) * mm, "construction": true});
            skLineSegment(sketch, "E88.MirrorCS", {"start": v(9.28, 10) * mm, "end": v(143.28, 10) * mm, "construction": true});
            skLineSegment(sketch, "E89.MirrorCS", {"start": v(128.78, 29) * mm, "end": v(143.28, 29) * mm});
            skLineSegment(sketch, "E90.MirrorCS", {"start": v(121.28, 21.5) * mm, "end": v(121.28, 10) * mm});
            skArc(sketch, "E91.MirrorCS", {"start": v(121.28, 21.5) * mm, "mid": v(123.47, 26.8) * mm, "end": v(128.78, 29) * mm});
            skLineSegment(sketch, "E92.MirrorCS", {"start": v(121.28, 138) * mm, "end": v(143.28, 138) * mm});
            skLineSegment(sketch, "E93.MirrorCS", {"start": v(143.28, 138) * mm, "end": v(121.28, 138) * mm, "construction": true});
            skLineSegment(sketch, "E94.MirrorCS", {"start": v(143.28, 138) * mm, "end": v(9.28, 138) * mm, "construction": true});
            skLineSegment(sketch, "E95.MirrorCS", {"start": v(31.28, 138) * mm, "end": v(9.28, 138) * mm});
            skLineSegment(sketch, "E96.MirrorCS", {"start": v(143.28, 119) * mm, "end": v(143.28, 138) * mm});
            skLineSegment(sketch, "E97.MirrorCS", {"start": v(9.28, 119) * mm, "end": v(9.28, 138) * mm});
            skLineSegment(sketch, "E98.MirrorCS", {"start": v(9.28, 138) * mm, "end": v(31.28, 138) * mm, "construction": true});
            skLineSegment(sketch, "E99.MirrorCS", {"start": v(31.28, 138) * mm, "end": v(121.28, 138) * mm, "construction": true});
            skLineSegment(sketch, "E100.MirrorCS", {"start": v(121.28, 138) * mm, "end": v(143.28, 138) * mm, "construction": true});
            skLineSegment(sketch, "E101.MirrorCS", {"start": v(31.28, 126.5) * mm, "end": v(31.28, 138) * mm});
            skLineSegment(sketch, "E102.MirrorCS", {"start": v(9.28, 119) * mm, "end": v(9.28, 138) * mm, "construction": true});
            skArc(sketch, "E103.MirrorCS", {"start": v(31.28, 126.5) * mm, "mid": v(29.08, 121.2) * mm, "end": v(23.78, 119) * mm});
            skLineSegment(sketch, "E104.MirrorCS", {"start": v(128.78, 119) * mm, "end": v(143.28, 119) * mm});
            skLineSegment(sketch, "E105.MirrorCS", {"start": v(9.28, 138) * mm, "end": v(143.28, 138) * mm, "construction": true});
            skLineSegment(sketch, "E106.MirrorCS", {"start": v(143.28, 119) * mm, "end": v(143.28, 138) * mm, "construction": true});
            skArc(sketch, "E107.MirrorCS", {"start": v(121.28, 126.5) * mm, "mid": v(123.47, 121.2) * mm, "end": v(128.78, 119) * mm});
            skLineSegment(sketch, "E108.MirrorCS", {"start": v(121.28, 126.5) * mm, "end": v(121.28, 138) * mm});
            skLineSegment(sketch, "E109.MirrorCS", {"start": v(23.78, 119) * mm, "end": v(9.28, 119) * mm});
            skCircle(sketch, "E110", {"center": v(23.78, 21.5) * mm, "radius": 2.25 * mm});
            skCircle(sketch, "E111", {"center": v(23.78, 126.5) * mm, "radius": 2.25 * mm});
            skCircle(sketch, "E112", {"center": v(128.78, 126.5) * mm, "radius": 2.25 * mm});
            skCircle(sketch, "E113", {"center": v(128.78, 21.5) * mm, "radius": 2.25 * mm});
            skSolve(sketch);
        }
        {
            var Q0;
            Q0 = qSketchRegion(id + "F36", true);
            extrude(context, id + "F37", {"entities" : qUnion([Q0]), "operationType" : NewBodyOperationType.ADD, "depth" : 10 * mm});
        }
        {
            var Q0;
            {var subQ1=sQuery(id+"F0.wireOp",EDGE,"E1.bottom");var subQ3=sQuery(id+"F0.wireOp",EDGE,"E1.right");var subQ4=sQuery(id+"F0.wireOp",EDGE,"E1.left");var subQ5=sQuery(id+"F0.wireOp",EDGE,"E1.top");var subQ6=sQuery(id+"F0.wireOp",EDGE,"E0.right");var subQ7=sQuery(id+"F0.wireOp",EDGE,"E0.left");var subQ8=sQuery(id+"F0.wireOp",EDGE,"E0.top");var subQ9=sQuery(id+"F0.wireOp",EDGE,"E0.bottom");var subQ17=makeQuery(id+"F1.opExtrude","SWEPT_FACE",FACE,{"disambiguationData":[OSD([subQ9])]});var subQ24=sQuery(id+"F8.wireOp",EDGE,"E30.bottom");var subQ25=sQuery(id+"F8.wireOp",EDGE,"E29.bottom");var subQ26=makeQuery(id+"F9.opExtrude","SWEPT_FACE",FACE,{"disambiguationData":[OSD([subQ25])]});var subQ28=makeQuery(id+"F1.opExtrude","CAP_FACE",FACE,{"disambiguationData":[OSD([subQ9,subQ8,subQ7,subQ6,subQ1,subQ5,subQ4,subQ3])],"isStart":true});var subQ29=makeQuery(id+"F9.opExtrude","SWEPT_FACE",FACE,{"disambiguationData":[OSD([subQ24])]});var subQ38=sQuery(id+"F12.wireOp",EDGE,"E42.bottom");var subQ41=sQuery(id+"F14.wireOp",EDGE,"E43.bottom");Q0=makeQuery(id+"F37.boolean.opBoolean","MERGE",FACE,{"derivedFrom":[makeQuery(id+"F33.boolean.opBoolean","MERGE",FACE,{"derivedFrom":[makeQuery(id+"F26.boolean.opBoolean","MERGE",FACE,{"derivedFrom":[makeQuery(id+"F24.boolean.opBoolean","MERGE",FACE,{"derivedFrom":[makeQuery(id+"F21.boolean.opBoolean","SPLIT",FACE,{"disambiguationData":[TD([subQ17])],"derivedFrom":makeQuery(id+"F15.boolean.opBoolean","MERGE",FACE,{"derivedFrom":[makeQuery(id+"F13.boolean.opBoolean","MERGE",FACE,{"derivedFrom":[makeQuery(id+"F9.boolean.opBoolean","MERGE",FACE,{"derivedFrom":[subQ28,subQ26,subQ29]}),makeQuery(id+"F13.opExtrude","SWEPT_FACE",FACE,{"disambiguationData":[OSD([subQ38])]})]}),makeQuery(id+"F15.opExtrude","SWEPT_FACE",FACE,{"disambiguationData":[OSD([subQ41])]})]})}),makeQuery(id+"F24.opExtrude","SWEPT_FACE",FACE,{"disambiguationData":[OSD([sQuery(id+"F23.wireOp",EDGE,"E53.bottom")])]})]}),makeQuery(id+"F26.opExtrude","SWEPT_FACE",FACE,{"disambiguationData":[OSD([sQuery(id+"F25.wireOp",EDGE,"E54.bottom")])]})]}),makeQuery(id+"F33.opExtrude","SWEPT_FACE",FACE,{"disambiguationData":[OSD([sQuery(id+"F32.wireOp",EDGE,"E68.bottom")])]}),makeQuery(id+"F33.opExtrude","SWEPT_FACE",FACE,{"disambiguationData":[OSD([sQuery(id+"F32.wireOp",EDGE,"E69.bottom")])]})]}),makeQuery(id+"F37.opExtrude","CAP_FACE",FACE,{"disambiguationData":[OSD([sQuery(id+"F36.wireOp",EDGE,"E74"),sQuery(id+"F36.wireOp",EDGE,"E77"),sQuery(id+"F36.wireOp",EDGE,"E78"),sQuery(id+"F36.wireOp",EDGE,"E79"),sQuery(id+"F36.wireOp",EDGE,"E80"),sQuery(id+"F36.wireOp",EDGE,"E110")])],"isStart":true}),makeQuery(id+"F37.opExtrude","CAP_FACE",FACE,{"disambiguationData":[OSD([sQuery(id+"F36.wireOp",EDGE,"E83.MirrorCS"),sQuery(id+"F36.wireOp",EDGE,"E84.MirrorCS"),sQuery(id+"F36.wireOp",EDGE,"E89.MirrorCS"),sQuery(id+"F36.wireOp",EDGE,"E90.MirrorCS"),sQuery(id+"F36.wireOp",EDGE,"E91.MirrorCS"),sQuery(id+"F36.wireOp",EDGE,"E113")])],"isStart":true}),makeQuery(id+"F37.opExtrude","CAP_FACE",FACE,{"disambiguationData":[OSD([sQuery(id+"F36.wireOp",EDGE,"E92.MirrorCS"),sQuery(id+"F36.wireOp",EDGE,"E96.MirrorCS"),sQuery(id+"F36.wireOp",EDGE,"E104.MirrorCS"),sQuery(id+"F36.wireOp",EDGE,"E107.MirrorCS"),sQuery(id+"F36.wireOp",EDGE,"E108.MirrorCS"),sQuery(id+"F36.wireOp",EDGE,"E112")])],"isStart":true}),makeQuery(id+"F37.opExtrude","CAP_FACE",FACE,{"disambiguationData":[OSD([sQuery(id+"F36.wireOp",EDGE,"E95.MirrorCS"),sQuery(id+"F36.wireOp",EDGE,"E97.MirrorCS"),sQuery(id+"F36.wireOp",EDGE,"E101.MirrorCS"),sQuery(id+"F36.wireOp",EDGE,"E103.MirrorCS"),sQuery(id+"F36.wireOp",EDGE,"E109.MirrorCS"),sQuery(id+"F36.wireOp",EDGE,"E111")])],"isStart":true})]});}
            var sketch = newSketch(context, id + "F38", { "sketchPlane" : qUnion([Q0])});
            skCircle(sketch, "E114.cCircle", {"center": v(23.78, -21.5) * mm, "radius": 3.5 * mm, "construction": true});
            skLineSegment(sketch, "E114.0", {"start": v(21.76, -18) * mm, "end": v(25.8, -18) * mm});
            skLineSegment(sketch, "E114.1", {"start": v(25.8, -18) * mm, "end": v(27.82, -21.5) * mm});
            skLineSegment(sketch, "E114.2", {"start": v(27.82, -21.5) * mm, "end": v(25.8, -25) * mm});
            skLineSegment(sketch, "E114.3", {"start": v(25.8, -25) * mm, "end": v(21.76, -25) * mm});
            skLineSegment(sketch, "E114.4", {"start": v(21.76, -25) * mm, "end": v(19.74, -21.5) * mm});
            skLineSegment(sketch, "E114.5", {"start": v(19.74, -21.5) * mm, "end": v(21.76, -18) * mm});
            skPoint(sketch, "E114.0.midPoint", {"position": v(23.78, -18) * mm});
            skLineSegment(sketch, "E115", {"start": v(76.28, -10) * mm, "end": v(76.28, -138) * mm, "construction": true});
            skLineSegment(sketch, "E116", {"start": v(9.28, -74) * mm, "end": v(143.8, -74) * mm, "construction": true});
            skPoint(sketch, "E116.endSnap0", {"position": v(76.28, -74) * mm});
            skLineSegment(sketch, "E117.MirrorCS", {"start": v(124.74, -21.5) * mm, "end": v(126.76, -25) * mm});
            skLineSegment(sketch, "E118.MirrorCS", {"start": v(126.76, -18) * mm, "end": v(124.74, -21.5) * mm});
            skLineSegment(sketch, "E119.MirrorCS", {"start": v(132.82, -21.5) * mm, "end": v(130.8, -18) * mm});
            skLineSegment(sketch, "E120.MirrorCS", {"start": v(130.8, -18) * mm, "end": v(126.76, -18) * mm});
            skLineSegment(sketch, "E121.MirrorCS", {"start": v(126.76, -25) * mm, "end": v(130.8, -25) * mm});
            skLineSegment(sketch, "E122.MirrorCS", {"start": v(130.8, -25) * mm, "end": v(132.82, -21.5) * mm});
            skCircle(sketch, "E123.MirrorC", {"center": v(128.78, -21.5) * mm, "radius": 3.5 * mm, "construction": true});
            skPoint(sketch, "E124.MirrorP", {"position": v(128.78, -18) * mm});
            skLineSegment(sketch, "E125.MirrorCS", {"start": v(130.8, -130) * mm, "end": v(126.76, -130) * mm});
            skLineSegment(sketch, "E126.MirrorCS", {"start": v(132.82, -126.5) * mm, "end": v(130.8, -130) * mm});
            skLineSegment(sketch, "E127.MirrorCS", {"start": v(126.76, -130) * mm, "end": v(124.74, -126.5) * mm});
            skCircle(sketch, "E128.MirrorC", {"center": v(128.78, -126.5) * mm, "radius": 3.5 * mm, "construction": true});
            skPoint(sketch, "E129.MirrorP", {"position": v(128.78, -130) * mm});
            skLineSegment(sketch, "E130.MirrorCS", {"start": v(124.74, -126.5) * mm, "end": v(126.76, -123) * mm});
            skLineSegment(sketch, "E131.MirrorCS", {"start": v(126.76, -123) * mm, "end": v(130.8, -123) * mm});
            skLineSegment(sketch, "E132.MirrorCS", {"start": v(130.8, -123) * mm, "end": v(132.82, -126.5) * mm});
            skLineSegment(sketch, "E133.MirrorCS", {"start": v(27.82, -126.5) * mm, "end": v(25.8, -123) * mm});
            skLineSegment(sketch, "E134.MirrorCS", {"start": v(25.8, -130) * mm, "end": v(27.82, -126.5) * mm});
            skLineSegment(sketch, "E135.MirrorCS", {"start": v(21.76, -123) * mm, "end": v(19.74, -126.5) * mm});
            skLineSegment(sketch, "E136.MirrorCS", {"start": v(21.76, -130) * mm, "end": v(25.8, -130) * mm});
            skLineSegment(sketch, "E137.MirrorCS", {"start": v(25.8, -123) * mm, "end": v(21.76, -123) * mm});
            skLineSegment(sketch, "E138.MirrorCS", {"start": v(19.74, -126.5) * mm, "end": v(21.76, -130) * mm});
            skPoint(sketch, "E139.MirrorP", {"position": v(23.78, -130) * mm});
            skCircle(sketch, "E140.MirrorC", {"center": v(23.78, -126.5) * mm, "radius": 3.5 * mm, "construction": true});
            skSolve(sketch);
        }
        {
            var Q0;
            Q0 = qSketchRegion(id + "F38", true);
            extrude(context, id + "F39", {"entities" : qUnion([Q0]), "operationType" : NewBodyOperationType.REMOVE, "oppositeDirection" : true, "depth" : 5 * mm});
        }
    });
